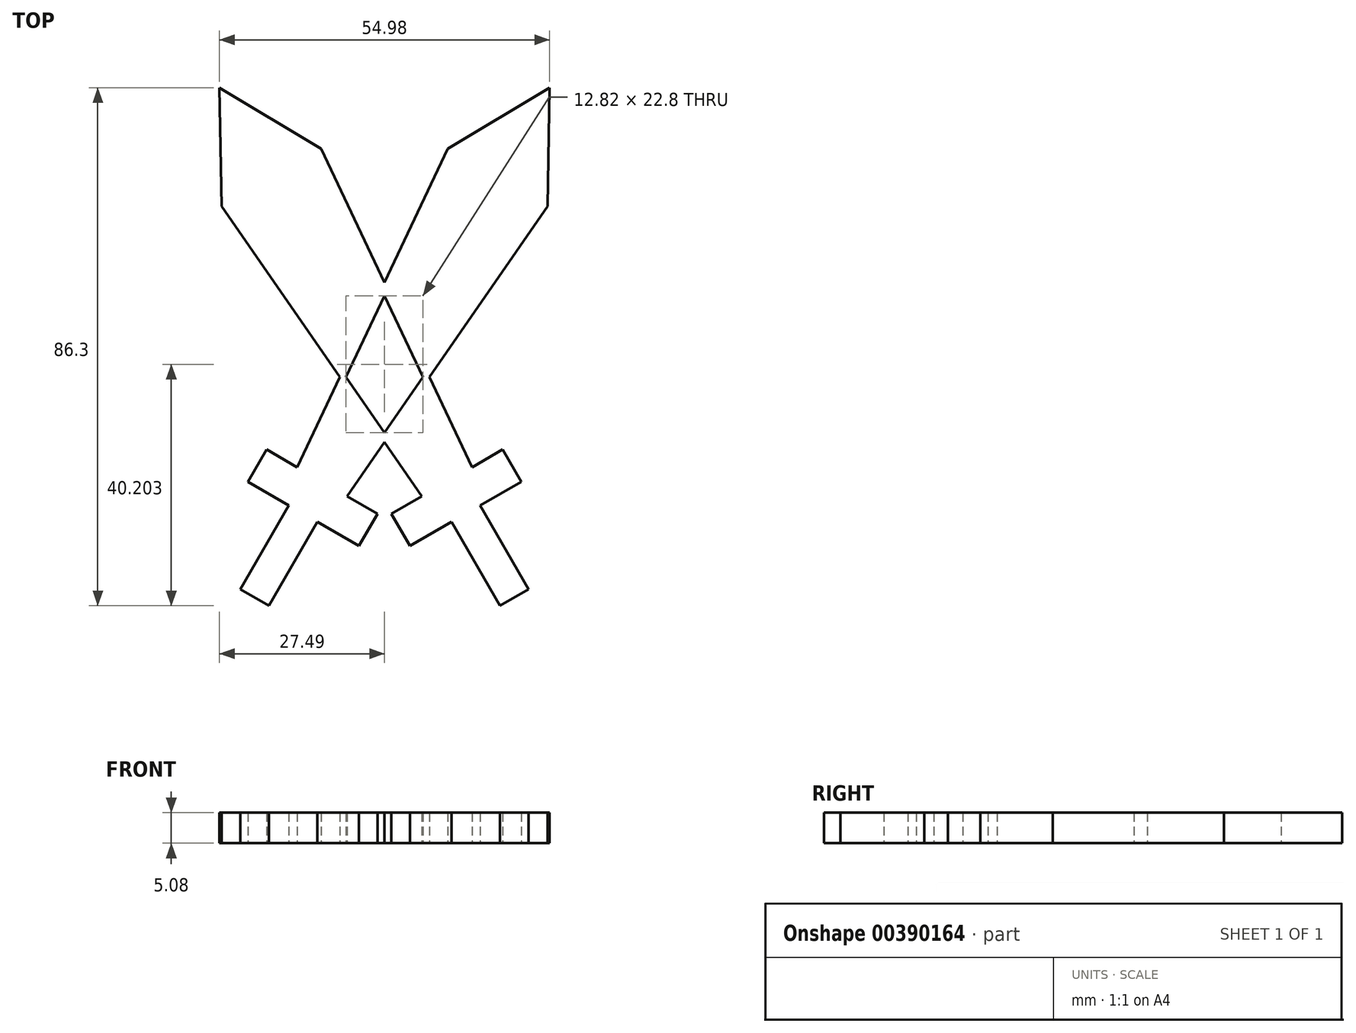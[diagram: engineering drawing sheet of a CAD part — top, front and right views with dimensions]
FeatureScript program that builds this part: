
annotation { "Feature Type Name" : "Feature", "Feature Type Description" : "" }
export const myFeature = defineFeature(function(context is Context, id is Id, definition is map)
    precondition{}
    {
        {
            var Q0;
            Q0=qCreatedBy(makeId("Top.planeOp"),FACE);
            var sketch = newSketch(context, id + "F0", { "sketchPlane" : qUnion([Q0])});
            skLineSegment(sketch, "E0.bottom", {"start": v(-22.76, -18.4) * mm, "end": v(-19.66, -13.03) * mm});
            skLineSegment(sketch, "E0.top", {"start": v(-4.25, -29.09) * mm, "end": v(-1.15, -23.72) * mm});
            skLineSegment(sketch, "E0.left", {"start": v(-22.76, -18.4) * mm, "end": v(-4.25, -29.09) * mm});
            skLineSegment(sketch, "E0.right", {"start": v(-19.66, -13.03) * mm, "end": v(-1.15, -23.72) * mm});
            skLineSegment(sketch, "E1", {"start": v(10.56, 37.09) * mm, "end": v(27.49, 47.26) * mm});
            skLineSegment(sketch, "E2.MirrorCS", {"start": v(27.14, 27.51) * mm, "end": v(27.49, 47.26) * mm});
            skLineSegment(sketch, "E3", {"start": v(10.56, 37.09) * mm, "end": v(-14.58, -15.97) * mm});
            skLineSegment(sketch, "E4.MirrorCS", {"start": v(27.14, 27.51) * mm, "end": v(-6.23, -20.78) * mm});
            skLineSegment(sketch, "E5.top", {"start": v(-23.98, -36.3) * mm, "end": v(-19.25, -39.04) * mm});
            skLineSegment(sketch, "E5.left", {"start": v(-15.92, -22.35) * mm, "end": v(-23.98, -36.3) * mm});
            skLineSegment(sketch, "E5.right", {"start": v(-11.19, -25.08) * mm, "end": v(-19.25, -39.04) * mm});
            skLineSegment(sketch, "E6.MirrorCS", {"start": v(-10.56, 37.09) * mm, "end": v(-27.49, 47.26) * mm});
            skLineSegment(sketch, "E7.MirrorCS", {"start": v(-27.14, 27.51) * mm, "end": v(-27.49, 47.26) * mm});
            skLineSegment(sketch, "E8.MirrorCS", {"start": v(-10.56, 37.09) * mm, "end": v(14.58, -15.97) * mm});
            skLineSegment(sketch, "E9.MirrorCS", {"start": v(-27.14, 27.51) * mm, "end": v(6.23, -20.78) * mm});
            skLineSegment(sketch, "E10.MirrorCS", {"start": v(19.66, -13.03) * mm, "end": v(1.15, -23.72) * mm});
            skLineSegment(sketch, "E11.MirrorCS", {"start": v(4.25, -29.09) * mm, "end": v(1.15, -23.72) * mm});
            skLineSegment(sketch, "E12.MirrorCS", {"start": v(22.76, -18.4) * mm, "end": v(4.25, -29.09) * mm});
            skLineSegment(sketch, "E13.MirrorCS", {"start": v(22.76, -18.4) * mm, "end": v(19.66, -13.03) * mm});
            skLineSegment(sketch, "E14.MirrorCS", {"start": v(15.92, -22.35) * mm, "end": v(23.98, -36.3) * mm});
            skLineSegment(sketch, "E15.MirrorCS", {"start": v(11.19, -25.08) * mm, "end": v(19.25, -39.04) * mm});
            skLineSegment(sketch, "E16.MirrorCS", {"start": v(23.98, -36.3) * mm, "end": v(19.25, -39.04) * mm});
            skLineSegment(sketch, "E17", {"start": v(0, 12.56) * mm, "end": v(-6.4, -0.96) * mm});
            skLineSegment(sketch, "E18.MirrorCS", {"start": v(0, 12.56) * mm, "end": v(6.4, -0.96) * mm});
            skLineSegment(sketch, "E19", {"start": v(-6.4, -0.96) * mm, "end": v(0, -10.24) * mm});
            skLineSegment(sketch, "E20.MirrorCS", {"start": v(6.4, -0.96) * mm, "end": v(0, -10.24) * mm});
            skSolve(sketch);
        }
        {
            var Q0;
            {var subQ1=sQuery(id+"F0.wireOp",EDGE,"E6.MirrorCS");Q0=makeQuery(id+"F0.imprint","IMPRINT",FACE,{"disambiguationData":[TD([[makeQuery(id+"F0.imprint","IMPRINT",EDGE,{"derivedFrom":subQ1}),1.0]])]});}
            extrude(context, id + "F1", {"entities" : qUnion([Q0]), "depth" : 5.08 * mm});
        }
        {
            var Q0;
            {var subQ0=sQuery(id+"F0.wireOp",EDGE,"E3");var subQ1=sQuery(id+"F0.wireOp",EDGE,"E0.right");var subQ2=makeQuery(id+"F0.imprint","INTERSECT",VERTEX,{"derivedFrom":[subQ1,subQ0]});Q0=makeQuery(id+"F0.imprint","IMPRINT",FACE,{"disambiguationData":[TD([[makeQuery(id+"F0.imprint","IMPRINT",EDGE,{"disambiguationData":[TD([[subQ2,-1.0]])],"derivedFrom":subQ1}),1.0]])]});}
            extrude(context, id + "F2", {"entities" : qUnion([Q0]), "depth" : 5.08 * mm});
        }
        {
            var Q0;
            Q0=makeQuery(id+"F0.imprint","IMPRINT",FACE,{"disambiguationData":[TD([[makeQuery(id+"F0.imprint","IMPRINT",EDGE,{"derivedFrom":sQuery(id+"F0.wireOp",EDGE,"E17")}),-1.0]])]});
            extrude(context, id + "F3", {"entities" : qUnion([Q0]), "depth" : 5.08 * mm});
        }
        {
            var Q0;
            {var subQ1=sQuery(id+"F0.wireOp",EDGE,"E1");Q0=makeQuery(id+"F0.imprint","IMPRINT",FACE,{"disambiguationData":[TD([[makeQuery(id+"F0.imprint","IMPRINT",EDGE,{"derivedFrom":subQ1}),-1.0]])]});}
            extrude(context, id + "F4", {"entities" : qUnion([Q0]), "operationType" : NewBodyOperationType.ADD, "depth" : 5.08 * mm});
        }
        {
            var Q0;
            {var subQ0=sQuery(id+"F0.wireOp",EDGE,"E8.MirrorCS");var subQ1=sQuery(id+"F0.wireOp",EDGE,"E4.MirrorCS");var subQ2=makeQuery(id+"F0.imprint","INTERSECT",VERTEX,{"derivedFrom":[subQ1,subQ0]});Q0=makeQuery(id+"F0.imprint","IMPRINT",FACE,{"disambiguationData":[TD([[makeQuery(id+"F0.imprint","IMPRINT",EDGE,{"disambiguationData":[TD([[subQ2,-1.0]])],"derivedFrom":subQ1}),1.0]])]});}
            extrude(context, id + "F5", {"entities" : qUnion([Q0]), "operationType" : NewBodyOperationType.ADD, "depth" : 5.08 * mm});
        }
        {
            var Q0;
            {var subQ0=sQuery(id+"F0.wireOp",EDGE,"E11.MirrorCS");Q0=makeQuery(id+"F0.imprint","IMPRINT",FACE,{"disambiguationData":[TD([[makeQuery(id+"F0.imprint","IMPRINT",EDGE,{"derivedFrom":subQ0}),-1.0]])]});}
            extrude(context, id + "F6", {"entities" : qUnion([Q0]), "operationType" : NewBodyOperationType.ADD, "depth" : 5.08 * mm});
        }
        {
            var Q0;
            {var subQ3=sQuery(id+"F0.wireOp",EDGE,"E0.bottom");Q0=makeQuery(id+"F0.imprint","IMPRINT",FACE,{"disambiguationData":[TD([[makeQuery(id+"F0.imprint","IMPRINT",EDGE,{"derivedFrom":subQ3}),-1.0]])]});}
            extrude(context, id + "F7", {"entities" : qUnion([Q0]), "operationType" : NewBodyOperationType.ADD, "depth" : 5.08 * mm});
        }
        {
            var Q0;
            Q0=makeQuery(id+"F0.imprint","IMPRINT",FACE,{"disambiguationData":[TD([[makeQuery(id+"F0.imprint","IMPRINT",EDGE,{"derivedFrom":sQuery(id+"F0.wireOp",EDGE,"E5.top")}),1.0]])]});
            extrude(context, id + "F8", {"entities" : qUnion([Q0]), "operationType" : NewBodyOperationType.ADD, "depth" : 5.08 * mm});
        }
        {
            var Q0;
            {var subQ0=sQuery(id+"F0.wireOp",EDGE,"E14.MirrorCS");Q0=makeQuery(id+"F0.imprint","IMPRINT",FACE,{"disambiguationData":[TD([[makeQuery(id+"F0.imprint","IMPRINT",EDGE,{"derivedFrom":subQ0}),-1.0]])]});}
            extrude(context, id + "F9", {"entities" : qUnion([Q0]), "operationType" : NewBodyOperationType.ADD, "depth" : 5.08 * mm});
        }
    });
